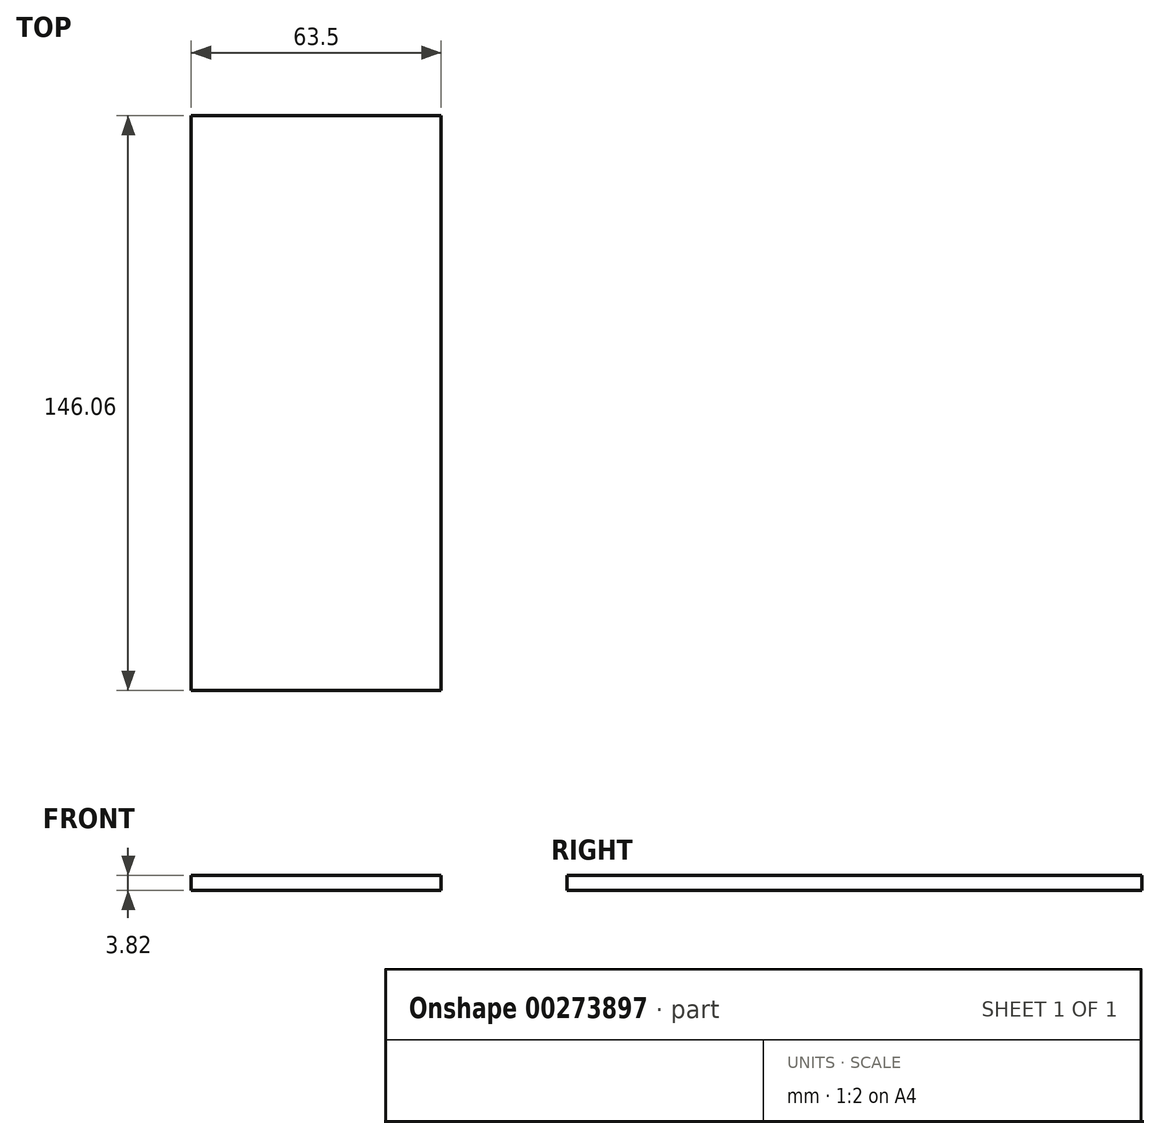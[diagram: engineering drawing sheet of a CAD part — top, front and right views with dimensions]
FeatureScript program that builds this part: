
annotation { "Feature Type Name" : "Feature", "Feature Type Description" : "" }
export const myFeature = defineFeature(function(context is Context, id is Id, definition is map)
    precondition{}
    {
        {
            var Q0;
            Q0=qCreatedBy(makeId("Top.planeOp"),FACE);
            var sketch = newSketch(context, id + "F0", { "sketchPlane" : qUnion([Q0])});
            skLineSegment(sketch, "E0.bottom", {"start": v(31.75, 73.03) * mm, "end": v(-31.75, 73.03) * mm});
            skLineSegment(sketch, "E0.top", {"start": v(31.75, -73.03) * mm, "end": v(-31.75, -73.03) * mm});
            skLineSegment(sketch, "E0.left", {"start": v(31.75, 73.03) * mm, "end": v(31.75, -73.03) * mm});
            skLineSegment(sketch, "E0.right", {"start": v(-31.75, 73.03) * mm, "end": v(-31.75, -73.03) * mm});
            skPoint(sketch, "E0.middle", {"position": v(0, 0) * mm});
            skSolve(sketch);
        }
        {
            var Q0;
            Q0=makeQuery(id+"F0.imprint","IMPRINT",FACE,{"disambiguationData":[TD([[makeQuery(id+"F0.imprint","IMPRINT",EDGE,{"derivedFrom":sQuery(id+"F0.wireOp",EDGE,"E0.bottom")}),1.0]])]});
            extrude(context, id + "F1", {"entities" : qUnion([Q0]), "endBound" : BoundingType.SYMMETRIC, "depth" : 3.8 * mm});
        }
    });
